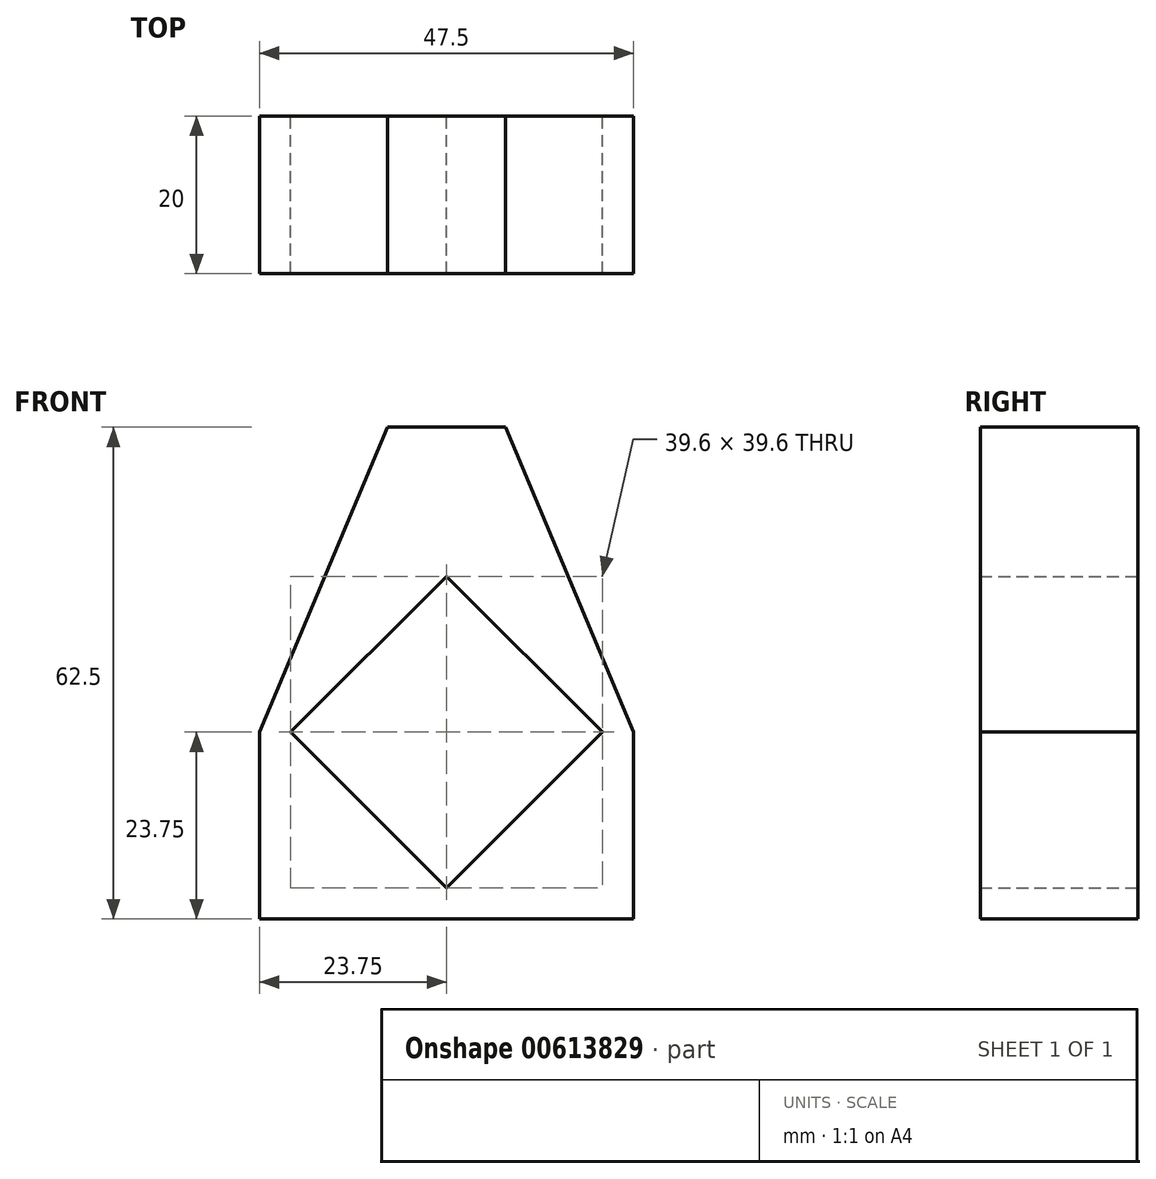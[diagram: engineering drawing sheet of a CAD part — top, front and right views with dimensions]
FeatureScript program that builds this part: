
annotation { "Feature Type Name" : "Feature", "Feature Type Description" : "" }
export const myFeature = defineFeature(function(context is Context, id is Id, definition is map)
    precondition{}
    {
        {
            var Q0;
            Q0=qCreatedBy(makeId("Front.planeOp"),FACE);
            var sketch = newSketch(context, id + "F0", { "sketchPlane" : qUnion([Q0])});
            skLineSegment(sketch, "E0.bottom", {"start": v(19.8, 19.8) * mm, "end": v(-19.8, 19.8) * mm});
            skLineSegment(sketch, "E0.top", {"start": v(19.8, -19.8) * mm, "end": v(-19.8, -19.8) * mm});
            skLineSegment(sketch, "E0.left", {"start": v(19.8, 19.8) * mm, "end": v(19.8, -19.8) * mm});
            skLineSegment(sketch, "E0.right", {"start": v(-19.8, 19.8) * mm, "end": v(-19.8, -19.8) * mm});
            skPoint(sketch, "E0.middle", {"position": v(0, 0) * mm});
            skLineSegment(sketch, "E1", {"start": v(0, 19.8) * mm, "end": v(19.8, 0) * mm});
            skLineSegment(sketch, "E2", {"start": v(19.8, 0) * mm, "end": v(0, -19.8) * mm});
            skLineSegment(sketch, "E3", {"start": v(0, -19.8) * mm, "end": v(-19.8, 0) * mm});
            skLineSegment(sketch, "E4", {"start": v(-19.8, 0) * mm, "end": v(0, 19.8) * mm});
            skLineSegment(sketch, "E5.bottom", {"start": v(23.75, 23.75) * mm, "end": v(-23.75, 23.75) * mm});
            skLineSegment(sketch, "E5.top", {"start": v(23.75, -23.75) * mm, "end": v(-23.75, -23.75) * mm});
            skLineSegment(sketch, "E5.left", {"start": v(23.75, 23.75) * mm, "end": v(23.75, -23.75) * mm});
            skLineSegment(sketch, "E5.right", {"start": v(-23.75, 23.75) * mm, "end": v(-23.75, -23.75) * mm});
            skSolve(sketch);
        }
        {
            var Q0;
            Q0 = qSketchRegion(id + "F0", true);
            var Q1;
            {var subQ3=sQuery(id+"F0.wireOp",EDGE,"E4");Q1=makeQuery(id+"F0.imprint","IMPRINT",FACE,{"disambiguationData":[TD([[makeQuery(id+"F0.imprint","IMPRINT",EDGE,{"derivedFrom":subQ3}),1.0]])]});}
            var Q2;
            {var subQ3=sQuery(id+"F0.wireOp",EDGE,"E3");Q2=makeQuery(id+"F0.imprint","IMPRINT",FACE,{"disambiguationData":[TD([[makeQuery(id+"F0.imprint","IMPRINT",EDGE,{"derivedFrom":subQ3}),1.0]])]});}
            var Q3;
            {var subQ3=sQuery(id+"F0.wireOp",EDGE,"E2");Q3=makeQuery(id+"F0.imprint","IMPRINT",FACE,{"disambiguationData":[TD([[makeQuery(id+"F0.imprint","IMPRINT",EDGE,{"derivedFrom":subQ3}),1.0]])]});}
            var Q4;
            {var subQ3=sQuery(id+"F0.wireOp",EDGE,"E1");Q4=makeQuery(id+"F0.imprint","IMPRINT",FACE,{"disambiguationData":[TD([[makeQuery(id+"F0.imprint","IMPRINT",EDGE,{"derivedFrom":subQ3}),1.0]])]});}
            extrude(context, id + "F1", {"entities" : qUnion([Q0, Q1, Q2, Q3, Q4]), "depth" : 20 * mm, "offsetDistance" : 25 * mm});
        }
        {
            var Q0;
            Q0=makeQuery(id+"F1.opExtrude","SWEPT_FACE",FACE,{"disambiguationData":[OSD([sQuery(id+"F0.wireOp",EDGE,"E5.bottom")])]});
            extrude(context, id + "F2", {"entities" : qUnion([Q0]), "operationType" : NewBodyOperationType.ADD, "depth" : 15 * mm, "offsetDistance" : 25 * mm});
        }
        {
            var Q0;
            {var subQ0=sQuery(id+"F0.wireOp",EDGE,"E5.bottom");Q0=makeQuery(id+"F2.boolean.opBoolean","MERGE",FACE,{"derivedFrom":[makeQuery(id+"F1.opExtrude","CAP_FACE",FACE,{"disambiguationData":[OSD([sQuery(id+"F0.wireOp",EDGE,"E1"),sQuery(id+"F0.wireOp",EDGE,"E2"),sQuery(id+"F0.wireOp",EDGE,"E3"),sQuery(id+"F0.wireOp",EDGE,"E4"),subQ0,sQuery(id+"F0.wireOp",EDGE,"E5.top"),sQuery(id+"F0.wireOp",EDGE,"E5.left"),sQuery(id+"F0.wireOp",EDGE,"E5.right")])],"isStart":false}),makeQuery(id+"F2.opExtrude","SWEPT_FACE",FACE,{"disambiguationData":[OSD([subQ0]),TDD([makeQuery(id+"F1.opExtrude","CAP_EDGE",EDGE,{"disambiguationData":[OSD([subQ0])],"isStart":false})])]})]});}
            var sketch = newSketch(context, id + "F3", { "sketchPlane" : qUnion([Q0])});
            skLineSegment(sketch, "E6", {"start": v(-23.75, 0) * mm, "end": v(-7.5, 38.75) * mm});
            skLineSegment(sketch, "E7", {"start": v(23.75, 0) * mm, "end": v(7.5, 38.75) * mm});
            skLineSegment(sketch, "E8", {"start": v(-7.5, 38.75) * mm, "end": v(-23.75, 38.75) * mm});
            skLineSegment(sketch, "E9", {"start": v(7.5, 38.75) * mm, "end": v(23.75, 38.75) * mm});
            skSolve(sketch);
        }
        {
            var Q0;
            Q0 = qSketchRegion(id + "F3", true);
            var Q1;
            {var subQ0=sQuery(id+"F3.wireOp",EDGE,"E6");Q1=makeQuery(id+"F3.imprint","IMPRINT",FACE,{"disambiguationData":[TD([[makeQuery(id+"F3.imprint","IMPRINT",EDGE,{"derivedFrom":subQ0}),1.0]])]});}
            var Q2;
            {var subQ0=sQuery(id+"F3.wireOp",EDGE,"E7");Q2=makeQuery(id+"F3.imprint","IMPRINT",FACE,{"disambiguationData":[TD([[makeQuery(id+"F3.imprint","IMPRINT",EDGE,{"derivedFrom":subQ0}),-1.0]])]});}
            extrude(context, id + "F4", {"entities" : qUnion([Q0, Q1, Q2]), "operationType" : NewBodyOperationType.REMOVE, "endBound" : BoundingType.THROUGH_ALL, "oppositeDirection" : true, "depth" : 25 * mm, "offsetDistance" : 25 * mm});
        }
    });
